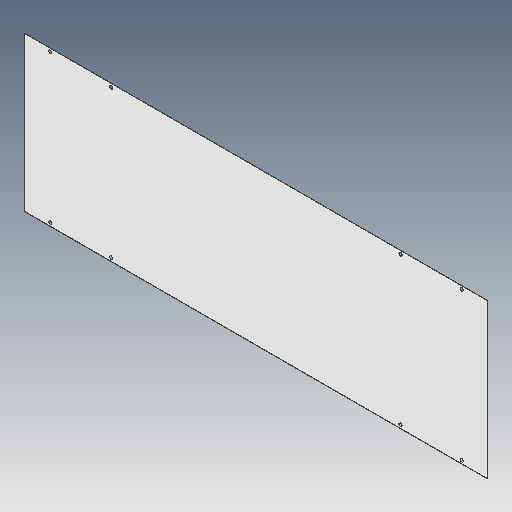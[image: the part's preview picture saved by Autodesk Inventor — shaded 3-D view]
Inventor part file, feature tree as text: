
AUTODESK INVENTOR PART (.ipt)
format: ipt  version: 2023.5 (Build 275446000, 446)  size: 90,112 bytes
history: native  units: in
note: dims shown in document units (in); Inventor stores cm internally (conversion verified against a paired STEP export)
features: mirror x1
ambient origin geometry x8: Origin, YZ Plane, XZ Plane, XY Plane, X Axis, Y Axis, Z Axis, Center Point
bodies: Solid1 (feature_tree)
feature tree (1):
  mirror  "Mirror1"
